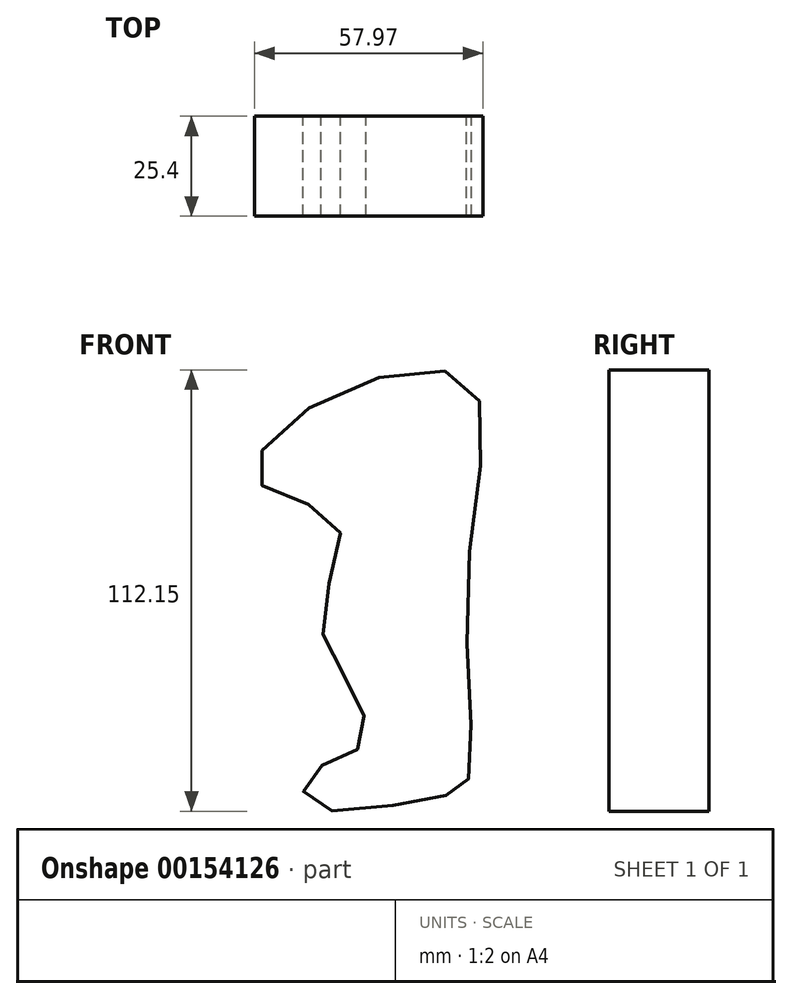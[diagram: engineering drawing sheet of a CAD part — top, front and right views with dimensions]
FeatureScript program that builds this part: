
annotation { "Feature Type Name" : "Feature", "Feature Type Description" : "" }
export const myFeature = defineFeature(function(context is Context, id is Id, definition is map)
    precondition{}
    {
        {
            var Q0;
            Q0=qCreatedBy(makeId("Front.planeOp"),FACE);
            var sketch = newSketch(context, id + "F0", { "sketchPlane" : qUnion([Q0])});
            skFitSpline(sketch, "E0", {"points": [v(-40.26, 42.24) * mm, v(-53.13, 23.56) * mm, v(-33.2, 13.18) * mm, v(-37.15, -11.31) * mm, v(-28.43, -30.4) * mm, v(-27.4, -43.9) * mm, v(-40.06, -50.54) * mm, v(-39.64, -58.63) * mm, v(-8.92, -56.76) * mm, v(0, -52.61) * mm, v(0, 0) * mm, v(0, 49.09) * mm, v(-40.26, 42.24) * mm]});
            skSolve(sketch);
        }
        {
            var Q0;
            Q0 = qSketchRegion(id + "F0", true);
            extrude(context, id + "F1", {"entities" : qUnion([Q0]), "depth" : 25.4 * mm});
        }
    });
